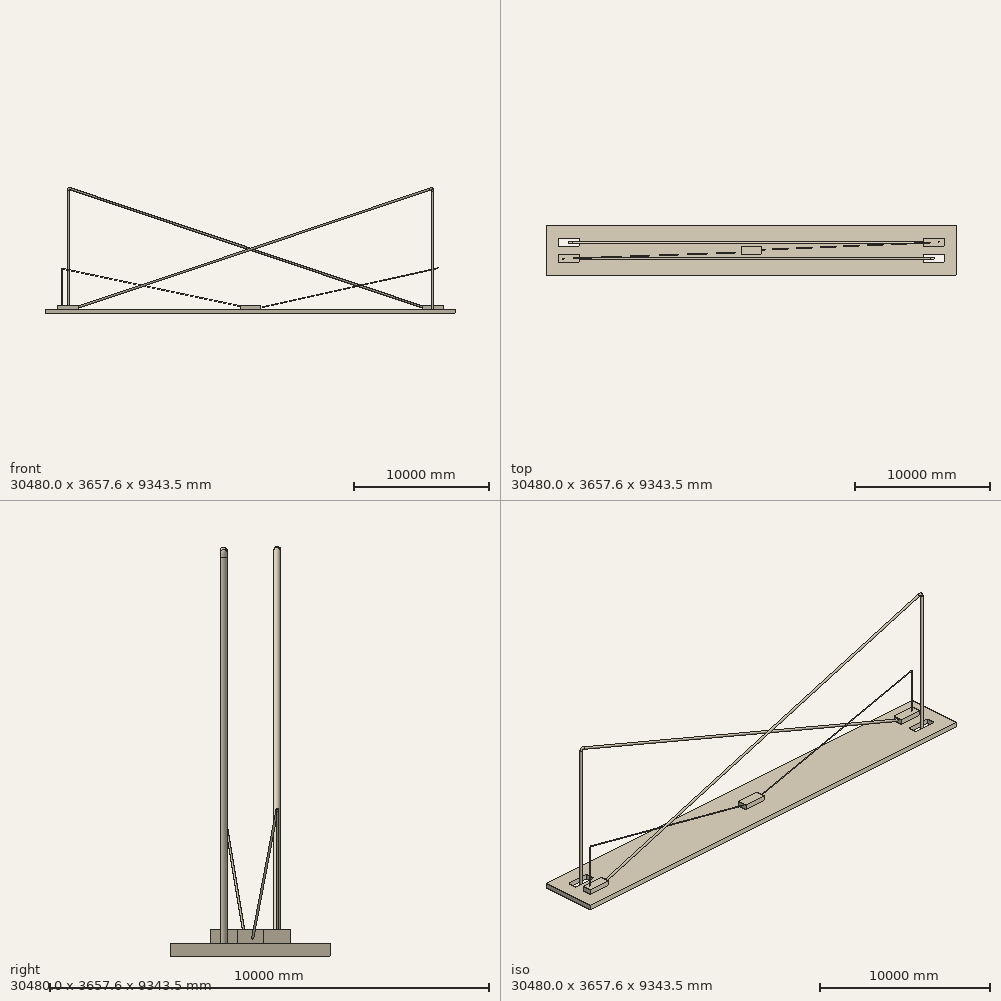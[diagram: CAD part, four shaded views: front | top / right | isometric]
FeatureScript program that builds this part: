
annotation { "Feature Type Name" : "Feature", "Feature Type Description" : "" }
export const myFeature = defineFeature(function(context is Context, id is Id, definition is map)
    precondition{}
    {
        {
            var Q0;
            Q0=qCreatedBy(makeId("Top.planeOp"),FACE);
            var sketch = newSketch(context, id + "F0", { "sketchPlane" : qUnion([Q0])});
            skLineSegment(sketch, "E0.bottom", {"start": v(15240, -1828.8) * mm, "end": v(-15240, -1828.8) * mm});
            skLineSegment(sketch, "E0.top", {"start": v(15240, 1828.8) * mm, "end": v(-15240, 1828.8) * mm});
            skLineSegment(sketch, "E0.left", {"start": v(15240, -1828.8) * mm, "end": v(15240, 1828.8) * mm});
            skLineSegment(sketch, "E0.right", {"start": v(-15240, -1828.8) * mm, "end": v(-15240, 1828.8) * mm});
            skPoint(sketch, "E0.middle", {"position": v(0, 0) * mm});
            skSolve(sketch);
        }
        {
            var Q0;
            Q0 = qSketchRegion(id + "F0", true);
            extrude(context, id + "F1", {"entities" : qUnion([Q0]), "depth" : 304.8 * mm, "offsetDistance" : 25.4 * mm});
        }
        {
            var Q0;
            Q0=makeQuery(id+"F1.opExtrude","CAP_FACE",FACE,{"disambiguationData":[OSD([sQuery(id+"F0.wireOp",EDGE,"E0.bottom"),sQuery(id+"F0.wireOp",EDGE,"E0.top"),sQuery(id+"F0.wireOp",EDGE,"E0.left"),sQuery(id+"F0.wireOp",EDGE,"E0.right")])],"isStart":false});
            var sketch = newSketch(context, id + "F2", { "sketchPlane" : qUnion([Q0])});
            skLineSegment(sketch, "E1", {"start": v(-17977.46, 914.4) * mm, "end": v(18300.4, 914.4) * mm, "construction": true});
            skLineSegment(sketch, "E2", {"start": v(-18010.1, -914.4) * mm, "end": v(18389.17, -914.4) * mm, "construction": true});
            skLineSegment(sketch, "E3", {"start": v(14325.6, 2510.02) * mm, "end": v(14325.6, -3119.62) * mm, "construction": true});
            skLineSegment(sketch, "E4", {"start": v(-14325.6, 2567.98) * mm, "end": v(-14325.6, -2658.46) * mm, "construction": true});
            skLineSegment(sketch, "E5.bottom", {"start": v(-14325.6, 914.4) * mm, "end": v(-12801.6, 914.4) * mm});
            skLineSegment(sketch, "E5.top", {"start": v(-14325.6, 304.8) * mm, "end": v(-12801.6, 304.8) * mm});
            skLineSegment(sketch, "E5.left", {"start": v(-14325.6, 914.4) * mm, "end": v(-14325.6, 304.8) * mm});
            skLineSegment(sketch, "E5.right", {"start": v(-12801.6, 914.4) * mm, "end": v(-12801.6, 304.8) * mm});
            skLineSegment(sketch, "E6.bottom", {"start": v(14325.6, -304.8) * mm, "end": v(12801.6, -304.8) * mm});
            skLineSegment(sketch, "E6.top", {"start": v(14325.6, -914.4) * mm, "end": v(12801.6, -914.4) * mm});
            skLineSegment(sketch, "E6.left", {"start": v(14325.6, -304.8) * mm, "end": v(14325.6, -914.4) * mm});
            skLineSegment(sketch, "E6.right", {"start": v(12801.6, -304.8) * mm, "end": v(12801.6, -914.4) * mm});
            skLineSegment(sketch, "E7.bottom", {"start": v(12801.6, 914.4) * mm, "end": v(14325.6, 914.4) * mm, "construction": true});
            skLineSegment(sketch, "E7.top", {"start": v(12801.6, 304.8) * mm, "end": v(14325.6, 304.8) * mm, "construction": true});
            skLineSegment(sketch, "E7.left", {"start": v(12801.6, 914.4) * mm, "end": v(12801.6, 304.8) * mm, "construction": true});
            skLineSegment(sketch, "E7.right", {"start": v(14325.6, 914.4) * mm, "end": v(14325.6, 304.8) * mm, "construction": true});
            skLineSegment(sketch, "E8.bottom", {"start": v(-14325.6, -304.8) * mm, "end": v(-12801.6, -304.8) * mm, "construction": true});
            skLineSegment(sketch, "E8.top", {"start": v(-14325.6, -914.4) * mm, "end": v(-12801.6, -914.4) * mm, "construction": true});
            skLineSegment(sketch, "E8.left", {"start": v(-14325.6, -304.8) * mm, "end": v(-14325.6, -914.4) * mm, "construction": true});
            skLineSegment(sketch, "E8.right", {"start": v(-12801.6, -304.8) * mm, "end": v(-12801.6, -914.4) * mm, "construction": true});
            skLineSegment(sketch, "E9.bottom", {"start": v(762, -304.8) * mm, "end": v(-762, -304.8) * mm});
            skLineSegment(sketch, "E9.top", {"start": v(762, 304.8) * mm, "end": v(-762, 304.8) * mm});
            skLineSegment(sketch, "E9.left", {"start": v(762, -304.8) * mm, "end": v(762, 304.8) * mm});
            skLineSegment(sketch, "E9.right", {"start": v(-762, -304.8) * mm, "end": v(-762, 304.8) * mm});
            skPoint(sketch, "E9.middle", {"position": v(0, 0) * mm});
            skLineSegment(sketch, "E10", {"start": v(12801.6, -609.6) * mm, "end": v(14325.6, -609.6) * mm, "construction": true});
            skLineSegment(sketch, "E11", {"start": v(13563.6, -304.8) * mm, "end": v(13563.6, -914.4) * mm, "construction": true});
            skSolve(sketch);
        }
        {
            var Q0;
            Q0 = qSketchRegion(id + "F2", true);
            extrude(context, id + "F3", {"entities" : qUnion([Q0]), "operationType" : NewBodyOperationType.REMOVE, "endBound" : BoundingType.THROUGH_ALL, "oppositeDirection" : true, "depth" : 25.4 * mm, "offsetDistance" : 25.4 * mm});
        }
        {
            var Q0;
            Q0=makeQuery(id+"F1.opExtrude","CAP_FACE",FACE,{"disambiguationData":[OSD([sQuery(id+"F0.wireOp",EDGE,"E0.bottom"),sQuery(id+"F0.wireOp",EDGE,"E0.top"),sQuery(id+"F0.wireOp",EDGE,"E0.left"),sQuery(id+"F0.wireOp",EDGE,"E0.right")])],"isStart":false});
            var sketch = newSketch(context, id + "F4", { "sketchPlane" : qUnion([Q0])});
            skLineSegment(sketch, "E12", {"start": v(-13563.6, 2097.28) * mm, "end": v(-13563.6, -1995.82) * mm, "construction": true});
            skLineSegment(sketch, "E13", {"start": v(-14593.28, 609.6) * mm, "end": v(-12270.27, 609.6) * mm, "construction": true});
            skCircle(sketch, "E14", {"center": v(-13563.6, 609.6) * mm, "radius": 76.2 * mm});
            skSolve(sketch);
        }
        {
            var Q0;
            Q0 = qSketchRegion(id + "F4", true);
            extrude(context, id + "F5", {"entities" : qUnion([Q0]), "depth" : 8839.2 * mm, "offsetDistance" : 25.4 * mm, "hasSecondDirection" : true, "secondDirectionOppositeDirection" : true, "secondDirectionDepth" : 304.8 * mm});
        }
        {
            var Q0;
            Q0=makeQuery(id+"F5.opExtrude","CAP_FACE",FACE,{"disambiguationData":[OSD([sQuery(id+"F4.wireOp",EDGE,"E14")])],"isStart":false});
            var sketch = newSketch(context, id + "F6", { "sketchPlane" : qUnion([Q0])});
            skLineSegment(sketch, "E15", {"start": v(-13563.6, 685.8) * mm, "end": v(-13563.6, 533.4) * mm, "construction": true});
            skLineSegment(sketch, "E16", {"start": v(-13639.8, 609.6) * mm, "end": v(-13487.4, 609.6) * mm, "construction": true});
            skSolve(sketch);
        }
        {
            var Q0;
            Q0=makeQuery(id+"F6.imprint","IMPRINT",FACE,{"disambiguationData":[TD([[makeQuery(id+"F6.imprint","IMPRINT",EDGE,{"derivedFrom":makeQuery(id+"F5.opExtrude","CAP_EDGE",EDGE,{"disambiguationData":[OSD([sQuery(id+"F4.wireOp",EDGE,"E14")])],"isStart":false})}),1.0]])]});
            var sketch = newSketch(context, id + "F7", { "sketchPlane" : qUnion([Q0])});
            skCircle(sketch, "E17", {"center": v(-13563.6, 609.6) * mm, "radius": 76.2 * mm});
            skSolve(sketch);
        }
        {
            var Q0;
            Q0=qCreatedBy(makeId("Front.planeOp"),FACE);
            cPlane(context, id + "F8", {"entities" : qUnion([Q0]), "cplaneType" : CPlaneType.OFFSET, "offset" : 609.6 * mm, "oppositeDirection" : true, "width" : 152.4 * mm, "height" : 152.4 * mm});
        }
        {
            var Q0;
            Q0=makeQuery(id+"F1.opExtrude","CAP_FACE",FACE,{"disambiguationData":[OSD([sQuery(id+"F0.wireOp",EDGE,"E0.bottom"),sQuery(id+"F0.wireOp",EDGE,"E0.top"),sQuery(id+"F0.wireOp",EDGE,"E0.left"),sQuery(id+"F0.wireOp",EDGE,"E0.right")])],"isStart":false});
            var sketch = newSketch(context, id + "F9", { "sketchPlane" : qUnion([Q0])});
            skLineSegment(sketch, "E18.bottom", {"start": v(12801.6, 914.4) * mm, "end": v(14325.6, 914.4) * mm});
            skLineSegment(sketch, "E18.top", {"start": v(12801.6, 304.8) * mm, "end": v(14325.6, 304.8) * mm});
            skLineSegment(sketch, "E18.left", {"start": v(12801.6, 914.4) * mm, "end": v(12801.6, 304.8) * mm});
            skLineSegment(sketch, "E18.right", {"start": v(14325.6, 914.4) * mm, "end": v(14325.6, 304.8) * mm});
            skSolve(sketch);
        }
        {
            var Q0;
            Q0=makeQuery(id+"F9.imprint","IMPRINT",FACE,{"disambiguationData":[TD([[makeQuery(id+"F9.imprint","IMPRINT",EDGE,{"derivedFrom":sQuery(id+"F9.wireOp",EDGE,"E18.bottom")}),-1.0]])]});
            extrude(context, id + "F10", {"entities" : qUnion([Q0]), "operationType" : NewBodyOperationType.ADD, "depth" : 304.8 * mm, "offsetDistance" : 25.4 * mm});
        }
        {
            var Q0;
            Q0=qCreatedBy(id+"F8.planeOp",FACE);
            var sketch = newSketch(context, id + "F11", { "sketchPlane" : qUnion([Q0])});
            skLineSegment(sketch, "E19", {"start": v(12795.68, 470.32) * mm, "end": v(-13306.6, 9230.54) * mm});
            skLineSegment(sketch, "E20", {"start": v(12795.68, 470.32) * mm, "end": v(11705.65, 470.32) * mm, "construction": true});
            skSolve(sketch);
        }
        {
            var Q0;
            Q0=makeQuery(id+"F10.opExtrude","SWEPT_FACE",FACE,{"disambiguationData":[OSD([sQuery(id+"F9.wireOp",EDGE,"E18.left")])]});
            var Q1;
            Q1=makeQuery(id+"F10.opExtrude","CAP_EDGE",EDGE,{"disambiguationData":[OSD([sQuery(id+"F9.wireOp",EDGE,"E18.left")])],"isStart":false});
            cPlane(context, id + "F12", {"entities" : qUnion([Q0, Q1]), "cplaneType" : CPlaneType.LINE_ANGLE, "offset" : 25.4 * mm, "angle" : 18.55 * degree, "oppositeDirection" : true, "width" : 152.4 * mm, "height" : 152.4 * mm});
        }
        {
            var Q0;
            Q0=qCreatedBy(id+"F12.planeOp",FACE);
            var sketch = newSketch(context, id + "F13", { "sketchPlane" : qUnion([Q0])});
            skCircle(sketch, "E21", {"center": v(609.6, 4516.6) * mm, "radius": 76.2 * mm});
            skSolve(sketch);
        }
        {
            var Q0;
            Q0=makeQuery(id+"F13.imprint","IMPRINT",FACE,{"disambiguationData":[TD([[makeQuery(id+"F13.imprint","IMPRINT",EDGE,{"derivedFrom":sQuery(id+"F13.wireOp",EDGE,"E21")}),1.0]])]});
            var Q1;
            Q1=makeQuery(id+"F10.opExtrude","SWEPT_FACE",FACE,{"disambiguationData":[OSD([sQuery(id+"F9.wireOp",EDGE,"E18.left")])]});
            extrude(context, id + "F14", {"entities" : qUnion([Q0]), "operationType" : NewBodyOperationType.ADD, "endBound" : BoundingType.UP_TO_SURFACE, "depth" : 25.4 * mm, "endBoundEntityFace" : qUnion([Q1]), "offsetDistance" : 25.4 * mm, "hasSecondDirection" : true, "secondDirectionOppositeDirection" : true, "secondDirectionDepth" : 27533.6 * mm});
        }
        {
            var Q0;
            Q0=makeQuery(id+"F14.opExtrude","CAP_FACE",FACE,{"disambiguationData":[OSD([sQuery(id+"F13.wireOp",EDGE,"E21")])],"isStart":true});
            var sketch = newSketch(context, id + "F15", { "sketchPlane" : qUnion([Q0])});
            skLineSegment(sketch, "E22", {"start": v(-609.6, 4592.8) * mm, "end": v(-609.6, 4440.4) * mm, "construction": true});
            skLineSegment(sketch, "E23", {"start": v(-685.8, 4516.6) * mm, "end": v(-533.4, 4516.6) * mm, "construction": true});
            skSolve(sketch);
        }
        {
            var Q0;
            Q0=qCreatedBy(id+"F8.planeOp",FACE);
            var sketch = newSketch(context, id + "F16", { "sketchPlane" : qUnion([Q0])});
            skFitSpline(sketch, "E24", {"points": [v(-13563.6, 9144) * mm, v(-13557.89, 9195.2) * mm, v(-13517.9, 9248.03) * mm, v(-13451.5, 9267.3) * mm, v(-13385.25, 9253.96) * mm, v(-13344.14, 9241.96) * mm], "startDerivative": vector(-5.95, 210.42) * mm, "endDerivative": vector(230.57, -66.68) * mm});
            skSolve(sketch);
        }
        {
            var Q0;
            Q0=makeQuery(id+"F7.imprint","IMPRINT",FACE,{"disambiguationData":[TD([[makeQuery(id+"F7.imprint","IMPRINT",EDGE,{"derivedFrom":sQuery(id+"F7.wireOp",EDGE,"E17")}),1.0]])]});
            var Q1;
            Q1=sQuery(id+"F16.wireOp",EDGE,"E24");
            sweep(context, id + "F17", {"profiles" : qUnion([Q0]), "path" : qUnion([Q1])});
        }
        {
            var Q0;
            Q0=makeQuery(id+"F10.opExtrude","CAP_FACE",FACE,{"disambiguationData":[OSD([sQuery(id+"F9.wireOp",EDGE,"E18.bottom"),sQuery(id+"F9.wireOp",EDGE,"E18.top"),sQuery(id+"F9.wireOp",EDGE,"E18.left"),sQuery(id+"F9.wireOp",EDGE,"E18.right")])],"isStart":false});
            var sketch = newSketch(context, id + "F18", { "sketchPlane" : qUnion([Q0])});
            skLineSegment(sketch, "E25", {"start": v(12801.6, 609.6) * mm, "end": v(14325.6, 609.6) * mm, "construction": true});
            skCircle(sketch, "E26", {"center": v(13970, 609.6) * mm, "radius": 25.4 * mm});
            skSolve(sketch);
        }
        {
            var Q0;
            Q0=makeQuery(id+"F18.imprint","IMPRINT",FACE,{"disambiguationData":[TD([[makeQuery(id+"F18.imprint","IMPRINT",EDGE,{"derivedFrom":sQuery(id+"F18.wireOp",EDGE,"E26")}),1.0]])]});
            var Q1;
            Q1 = qConstructionFilter(qBodyType(qCreatedBy(id + "F18" ,EDGE), BodyType.WIRE), ConstructionObject.NO);
            extrude(context, id + "F19", {"entities" : qUnion([Q0]), "surfaceEntities" : qUnion([Q1]), "depth" : 2692.4 * mm, "offsetDistance" : 25.4 * mm});
        }
        {
            var Q0;
            Q0=makeQuery(id+"F1.opExtrude","CAP_FACE",FACE,{"disambiguationData":[OSD([sQuery(id+"F0.wireOp",EDGE,"E0.bottom"),sQuery(id+"F0.wireOp",EDGE,"E0.top"),sQuery(id+"F0.wireOp",EDGE,"E0.left"),sQuery(id+"F0.wireOp",EDGE,"E0.right")])],"isStart":false});
            var sketch = newSketch(context, id + "F20", { "sketchPlane" : qUnion([Q0])});
            skLineSegment(sketch, "E27", {"start": v(12801.6, -609.6) * mm, "end": v(14325.6, -609.6) * mm, "construction": true});
            skLineSegment(sketch, "E28", {"start": v(13563.6, -304.8) * mm, "end": v(13563.6, -914.4) * mm, "construction": true});
            skCircle(sketch, "E29", {"center": v(13563.6, -609.6) * mm, "radius": 76.2 * mm});
            skSolve(sketch);
        }
        {
            var Q0;
            Q0 = qSketchRegion(id + "F20", true);
            extrude(context, id + "F21", {"entities" : qUnion([Q0]), "depth" : 8788.4 * mm, "offsetDistance" : 25.4 * mm, "hasSecondDirection" : true, "secondDirectionOppositeDirection" : true, "secondDirectionDepth" : 304.8 * mm});
        }
        {
            var Q0;
            Q0=makeQuery(id+"F1.opExtrude","CAP_FACE",FACE,{"disambiguationData":[OSD([sQuery(id+"F0.wireOp",EDGE,"E0.bottom"),sQuery(id+"F0.wireOp",EDGE,"E0.top"),sQuery(id+"F0.wireOp",EDGE,"E0.left"),sQuery(id+"F0.wireOp",EDGE,"E0.right")])],"isStart":false});
            var sketch = newSketch(context, id + "F22", { "sketchPlane" : qUnion([Q0])});
            skLineSegment(sketch, "E30.bottom", {"start": v(-14325.6, -304.8) * mm, "end": v(-12801.6, -304.8) * mm});
            skLineSegment(sketch, "E30.top", {"start": v(-14325.6, -914.4) * mm, "end": v(-12801.6, -914.4) * mm});
            skLineSegment(sketch, "E30.left", {"start": v(-14325.6, -304.8) * mm, "end": v(-14325.6, -914.4) * mm});
            skLineSegment(sketch, "E30.right", {"start": v(-12801.6, -304.8) * mm, "end": v(-12801.6, -914.4) * mm});
            skSolve(sketch);
        }
        {
            var Q0;
            Q0 = qSketchRegion(id + "F22", true);
            extrude(context, id + "F23", {"entities" : qUnion([Q0]), "operationType" : NewBodyOperationType.ADD, "depth" : 304.8 * mm, "offsetDistance" : 25.4 * mm});
        }
        {
            var Q0;
            Q0=makeQuery(id+"F23.opExtrude","SWEPT_FACE",FACE,{"disambiguationData":[OSD([sQuery(id+"F22.wireOp",EDGE,"E30.right")])]});
            var Q1;
            Q1=makeQuery(id+"F23.opExtrude","CAP_EDGE",EDGE,{"disambiguationData":[OSD([sQuery(id+"F22.wireOp",EDGE,"E30.right")])],"isStart":false});
            cPlane(context, id + "F24", {"entities" : qUnion([Q0, Q1]), "cplaneType" : CPlaneType.LINE_ANGLE, "offset" : 25.4 * mm, "angle" : 18.55 * degree, "width" : 152.4 * mm, "height" : 152.4 * mm});
        }
        {
            var Q0;
            Q0=qCreatedBy(id+"F8.planeOp",FACE);
            cPlane(context, id + "F25", {"entities" : qUnion([Q0]), "cplaneType" : CPlaneType.OFFSET, "offset" : 1219.2 * mm, "width" : 152.4 * mm, "height" : 152.4 * mm});
        }
        {
            var Q0;
            Q0=qCreatedBy(id+"F24.planeOp",FACE);
            var sketch = newSketch(context, id + "F26", { "sketchPlane" : qUnion([Q0])});
            skCircle(sketch, "E31", {"center": v(609.6, 4498.13) * mm, "radius": 76.2 * mm});
            skSolve(sketch);
        }
        {
            var Q0;
            Q0=makeQuery(id+"F26.imprint","IMPRINT",FACE,{"disambiguationData":[TD([[makeQuery(id+"F26.imprint","IMPRINT",EDGE,{"derivedFrom":sQuery(id+"F26.wireOp",EDGE,"E31")}),1.0]])]});
            var Q1;
            Q1=makeQuery(id+"F23.opExtrude","SWEPT_FACE",FACE,{"disambiguationData":[OSD([sQuery(id+"F22.wireOp",EDGE,"E30.right")])]});
            extrude(context, id + "F27", {"entities" : qUnion([Q0]), "operationType" : NewBodyOperationType.ADD, "oppositeDirection" : true, "depth" : 27508.2 * mm, "offsetDistance" : 25.4 * mm, "hasSecondDirection" : true, "secondDirectionBound" : SecondDirectionBoundingType.UP_TO_SURFACE, "secondDirectionOppositeDirection" : false, "secondDirectionDepth" : 25.4 * mm, "secondDirectionBoundEntityFace" : qUnion([Q1])});
        }
        {
            var Q0;
            Q0=makeQuery(id+"F21.opExtrude","CAP_FACE",FACE,{"disambiguationData":[OSD([sQuery(id+"F20.wireOp",EDGE,"E29")])],"isStart":false});
            var sketch = newSketch(context, id + "F28", { "sketchPlane" : qUnion([Q0])});
            skLineSegment(sketch, "E32", {"start": v(13563.6, -533.4) * mm, "end": v(13563.6, -685.8) * mm, "construction": true});
            skLineSegment(sketch, "E33", {"start": v(13487.4, -609.6) * mm, "end": v(13639.8, -609.6) * mm, "construction": true});
            skSolve(sketch);
        }
        {
            var Q0;
            {var subQ0=sQuery(id+"F26.wireOp",EDGE,"E31");Q0=makeQuery(id+"F27.opExtrude","CAP_FACE",FACE,{"disambiguationData":[OSD([subQ0]),topologyDisambiguationEdgeConnected([makeQuery(id+"F26.imprint","IMPRINT",EDGE,{"derivedFrom":subQ0})])],"isStart":false});}
            var sketch = newSketch(context, id + "F29", { "sketchPlane" : qUnion([Q0])});
            skLineSegment(sketch, "E34", {"start": v(-533.4, 4498.13) * mm, "end": v(-685.8, 4498.13) * mm, "construction": true});
            skLineSegment(sketch, "E35", {"start": v(-609.6, 4574.33) * mm, "end": v(-609.6, 4421.93) * mm, "construction": true});
            skSolve(sketch);
        }
        {
            var Q0;
            Q0=qCreatedBy(id+"F25.planeOp",FACE);
            var sketch = newSketch(context, id + "F30", { "sketchPlane" : qUnion([Q0])});
            skFitSpline(sketch, "E36", {"points": [v(13325.93, 9216.36) * mm, v(13389.39, 9235.5) * mm, v(13462.23, 9248.26) * mm, v(13530.33, 9233.42) * mm, v(13556.5, 9195.8) * mm, v(13562.3, 9149.55) * mm, v(13563.6, 9093.2) * mm], "startDerivative": vector(362.98, 130.88) * mm, "endDerivative": vector(2.68, -321.12) * mm});
            skSolve(sketch);
        }
        {
            var Q0;
            {var subQ0=sQuery(id+"F26.wireOp",EDGE,"E31");Q0=makeQuery(id+"F29.imprint","IMPRINT",FACE,{"disambiguationData":[TD([[makeQuery(id+"F29.imprint","IMPRINT",EDGE,{"derivedFrom":makeQuery(id+"F27.opExtrude","CAP_EDGE",EDGE,{"disambiguationData":[OSD([subQ0]),topologyDisambiguationEdgeConnected([makeQuery(id+"F26.imprint","IMPRINT",EDGE,{"derivedFrom":subQ0})])],"isStart":false})}),-1.0]])]});}
            var Q1;
            Q1=sQuery(id+"F30.wireOp",EDGE,"E36");
            sweep(context, id + "F31", {"profiles" : qUnion([Q0]), "path" : qUnion([Q1])});
        }
        {
            var Q0;
            Q0=makeQuery(id+"F1.opExtrude","CAP_FACE",FACE,{"disambiguationData":[OSD([sQuery(id+"F0.wireOp",EDGE,"E0.bottom"),sQuery(id+"F0.wireOp",EDGE,"E0.top"),sQuery(id+"F0.wireOp",EDGE,"E0.left"),sQuery(id+"F0.wireOp",EDGE,"E0.right")])],"isStart":false});
            var sketch = newSketch(context, id + "F32", { "sketchPlane" : qUnion([Q0])});
            skLineSegment(sketch, "E37.bottom", {"start": v(-762, -304.8) * mm, "end": v(762, -304.8) * mm});
            skLineSegment(sketch, "E37.top", {"start": v(-762, 304.8) * mm, "end": v(762, 304.8) * mm});
            skLineSegment(sketch, "E37.left", {"start": v(-762, -304.8) * mm, "end": v(-762, 304.8) * mm});
            skLineSegment(sketch, "E37.right", {"start": v(762, -304.8) * mm, "end": v(762, 304.8) * mm});
            skSolve(sketch);
        }
        {
            var Q0;
            Q0 = qSketchRegion(id + "F32", true);
            extrude(context, id + "F33", {"entities" : qUnion([Q0]), "depth" : 304.8 * mm, "offsetDistance" : 25.4 * mm});
        }
        {
            var Q0;
            Q0=makeQuery(id+"F19.opExtrude","CAP_FACE",FACE,{"disambiguationData":[OSD([sQuery(id+"F18.wireOp",EDGE,"E26")])],"isStart":false});
            var sketch = newSketch(context, id + "F34", { "sketchPlane" : qUnion([Q0])});
            skLineSegment(sketch, "E38", {"start": v(13944.6, 609.6) * mm, "end": v(13995.4, 609.6) * mm, "construction": true});
            skLineSegment(sketch, "E39", {"start": v(13968.93, 634.98) * mm, "end": v(13971.07, 584.22) * mm, "construction": true});
            skLineSegment(sketch, "E40", {"start": v(13995.38, 610.67) * mm, "end": v(13944.62, 608.53) * mm, "construction": true});
            skSolve(sketch);
        }
        {
            var Q0;
            Q0=makeQuery(id+"F34.imprint","IMPRINT",FACE,{"disambiguationData":[TD([[makeQuery(id+"F34.imprint","IMPRINT",EDGE,{"derivedFrom":makeQuery(id+"F19.opExtrude","CAP_EDGE",EDGE,{"disambiguationData":[OSD([sQuery(id+"F18.wireOp",EDGE,"E26")])],"isStart":false})}),1.0]])]});
            cPlane(context, id + "F35", {"entities" : qUnion([Q0]), "cplaneType" : CPlaneType.OFFSET, "offset" : 50.8 * mm, "width" : 152.4 * mm, "height" : 152.4 * mm});
        }
        {
            var Q0;
            Q0=qCreatedBy(id+"F35.planeOp",FACE);
            var sketch = newSketch(context, id + "F36", { "sketchPlane" : qUnion([Q0])});
            skLineSegment(sketch, "E41", {"start": v(13968.93, 634.98) * mm, "end": v(13971.07, 584.22) * mm, "construction": true});
            skSolve(sketch);
        }
        {
            var Q0;
            Q0=sQuery(id+"F36.wireOp",EDGE,"E41");
            var Q1;
            Q1=makeQuery(id+"F1.opExtrude","CAP_FACE",FACE,{"disambiguationData":[OSD([sQuery(id+"F0.wireOp",EDGE,"E0.bottom"),sQuery(id+"F0.wireOp",EDGE,"E0.top"),sQuery(id+"F0.wireOp",EDGE,"E0.left"),sQuery(id+"F0.wireOp",EDGE,"E0.right")])],"isStart":false});
            cPlane(context, id + "F37", {"entities" : qUnion([Q0, Q1]), "cplaneType" : CPlaneType.LINE_ANGLE, "offset" : 25.4 * mm, "angle" : 77.5 * degree, "oppositeDirection" : true, "width" : 152.4 * mm, "height" : 152.4 * mm});
        }
        {
            var Q0;
            Q0=sQuery(id+"F34.wireOp",EDGE,"E40");
            var Q1;
            Q1=makeQuery(id+"F1.opExtrude","CAP_FACE",FACE,{"disambiguationData":[OSD([sQuery(id+"F0.wireOp",EDGE,"E0.bottom"),sQuery(id+"F0.wireOp",EDGE,"E0.top"),sQuery(id+"F0.wireOp",EDGE,"E0.left"),sQuery(id+"F0.wireOp",EDGE,"E0.right")])],"isStart":false});
            cPlane(context, id + "F38", {"entities" : qUnion([Q0, Q1]), "cplaneType" : CPlaneType.LINE_ANGLE, "offset" : 25.4 * mm, "angle" : 90 * degree, "width" : 152.4 * mm, "height" : 152.4 * mm});
        }
        {
            var Q0;
            Q0=qCreatedBy(id+"F37.planeOp",FACE);
            cPlane(context, id + "F39", {"entities" : qUnion([Q0]), "cplaneType" : CPlaneType.OFFSET, "offset" : 50.8 * mm, "width" : 152.4 * mm, "height" : 152.4 * mm});
        }
        {
            var Q0;
            Q0=qCreatedBy(id+"F39.planeOp",FACE);
            var sketch = newSketch(context, id + "F40", { "sketchPlane" : qUnion([Q0])});
            skCircle(sketch, "E42", {"center": v(-16.92, 246.95) * mm, "radius": 25.4 * mm});
            skSolve(sketch);
        }
        {
            var Q0;
            Q0 = qSketchRegion(id + "F40", true);
            extrude(context, id + "F41", {"entities" : qUnion([Q0]), "operationType" : NewBodyOperationType.ADD, "endBound" : BoundingType.UP_TO_NEXT, "depth" : 25.4 * mm, "offsetDistance" : 25.4 * mm});
        }
        {
            var Q0;
            Q0=makeQuery(id+"F41.opExtrude","CAP_FACE",FACE,{"disambiguationData":[OSD([sQuery(id+"F40.wireOp",EDGE,"E42")])],"isStart":true});
            var sketch = newSketch(context, id + "F42", { "sketchPlane" : qUnion([Q0])});
            skLineSegment(sketch, "E43", {"start": v(-1.84, 264.08) * mm, "end": v(35.68, 229.83) * mm, "construction": true});
            skLineSegment(sketch, "E44", {"start": v(-0.2, 228.2) * mm, "end": v(34.05, 265.72) * mm, "construction": true});
            skSolve(sketch);
        }
        {
            var Q0;
            Q0=qCreatedBy(id+"F38.planeOp",FACE);
            var sketch = newSketch(context, id + "F43", { "sketchPlane" : qUnion([Q0])});
            skFitSpline(sketch, "E45", {"points": [v(13983.28, 3302) * mm, v(13980.36, 3327.16) * mm, v(13972.6, 3340.3) * mm, v(13960.9, 3345.86) * mm, v(13948.48, 3345.39) * mm, v(13933.69, 3341.8) * mm], "startDerivative": vector(-2.2, 65.07) * mm, "endDerivative": vector(-67.3, -13.02) * mm});
            skSolve(sketch);
        }
        {
            var Q0;
            Q0=makeQuery(id+"F34.imprint","IMPRINT",FACE,{"disambiguationData":[TD([[makeQuery(id+"F34.imprint","IMPRINT",EDGE,{"derivedFrom":makeQuery(id+"F19.opExtrude","CAP_EDGE",EDGE,{"disambiguationData":[OSD([sQuery(id+"F18.wireOp",EDGE,"E26")])],"isStart":false})}),1.0]])]});
            var Q1;
            Q1=sQuery(id+"F43.wireOp",EDGE,"E45");
            sweep(context, id + "F44", {"profiles" : qUnion([Q0]), "path" : qUnion([Q1])});
        }
        {
            var Q0;
            Q0=makeQuery(id+"F23.opExtrude","CAP_FACE",FACE,{"disambiguationData":[OSD([sQuery(id+"F22.wireOp",EDGE,"E30.bottom"),sQuery(id+"F22.wireOp",EDGE,"E30.top"),sQuery(id+"F22.wireOp",EDGE,"E30.left"),sQuery(id+"F22.wireOp",EDGE,"E30.right")])],"isStart":false});
            var sketch = newSketch(context, id + "F45", { "sketchPlane" : qUnion([Q0])});
            skCircle(sketch, "E46", {"center": v(-14020.8, -609.6) * mm, "radius": 25.4 * mm});
            skSolve(sketch);
        }
        {
            var Q0;
            Q0 = qSketchRegion(id + "F45", true);
            extrude(context, id + "F46", {"entities" : qUnion([Q0]), "operationType" : NewBodyOperationType.ADD, "depth" : 2667 * mm, "offsetDistance" : 25.4 * mm});
        }
        {
            var Q0;
            Q0=makeQuery(id+"F46.opExtrude","CAP_FACE",FACE,{"disambiguationData":[OSD([sQuery(id+"F45.wireOp",EDGE,"E46")])],"isStart":false});
            var sketch = newSketch(context, id + "F47", { "sketchPlane" : qUnion([Q0])});
            skLineSegment(sketch, "E47", {"start": v(-13995.4, -609.6) * mm, "end": v(-14046.2, -609.6) * mm, "construction": true});
            skLineSegment(sketch, "E48", {"start": v(-14020.92, -635) * mm, "end": v(-14020.92, -584.2) * mm, "construction": true});
            skLineSegment(sketch, "E49", {"start": v(-13995.42, -608.71) * mm, "end": v(-14046.18, -610.49) * mm, "construction": true});
            skSolve(sketch);
        }
        {
            var Q0;
            Q0=sQuery(id+"F47.wireOp",EDGE,"E48");
            var Q1;
            Q1=sQuery(id+"F47.wireOp",EDGE,"E47");
            cPlane(context, id + "F48", {"entities" : qUnion([Q0, Q1]), "cplaneType" : CPlaneType.LINE_ANGLE, "offset" : 25.4 * mm, "angle" : 90 * degree, "width" : 152.4 * mm, "height" : 152.4 * mm});
        }
        {
            var Q0;
            Q0=qCreatedBy(id+"F48.planeOp",FACE);
            var Q1;
            Q1=sQuery(id+"F47.wireOp",EDGE,"E49");
            cPlane(context, id + "F49", {"entities" : qUnion([Q0, Q1]), "cplaneType" : CPlaneType.LINE_ANGLE, "offset" : 25.4 * mm, "angle" : 0 * degree, "width" : 152.4 * mm, "height" : 152.4 * mm});
        }
        {
            var Q0;
            Q0=makeQuery(id+"F47.imprint","IMPRINT",FACE,{"disambiguationData":[TD([[makeQuery(id+"F47.imprint","IMPRINT",EDGE,{"derivedFrom":makeQuery(id+"F46.opExtrude","CAP_EDGE",EDGE,{"disambiguationData":[OSD([sQuery(id+"F45.wireOp",EDGE,"E46")])],"isStart":false})}),1.0]])]});
            cPlane(context, id + "F50", {"entities" : qUnion([Q0]), "cplaneType" : CPlaneType.OFFSET, "offset" : 50.8 * mm, "width" : 152.4 * mm, "height" : 152.4 * mm});
        }
        {
            var Q0;
            Q0=qCreatedBy(id+"F50.planeOp",FACE);
            var sketch = newSketch(context, id + "F51", { "sketchPlane" : qUnion([Q0])});
            skLineSegment(sketch, "E50", {"start": v(-14020.92, -635) * mm, "end": v(-14020.92, -584.2) * mm, "construction": true});
            skCircle(sketch, "E51", {"center": v(-14020.92, -609.6) * mm, "radius": 25.4 * mm, "construction": true});
            skLineSegment(sketch, "E52", {"start": v(-14020.04, -634.98) * mm, "end": v(-14021.8, -584.22) * mm, "construction": true});
            skSolve(sketch);
        }
        {
            var Q0;
            Q0=qCreatedBy(id+"F50.planeOp",FACE);
            var Q1;
            Q1=sQuery(id+"F51.wireOp",EDGE,"E52");
            cPlane(context, id + "F52", {"entities" : qUnion([Q0, Q1]), "cplaneType" : CPlaneType.LINE_ANGLE, "offset" : 25.4 * mm, "angle" : 78.11 * degree, "oppositeDirection" : true, "width" : 152.4 * mm, "height" : 152.4 * mm});
        }
        {
            var Q0;
            Q0=qCreatedBy(id+"F52.planeOp",FACE);
            cPlane(context, id + "F53", {"entities" : qUnion([Q0]), "cplaneType" : CPlaneType.OFFSET, "offset" : 63.5 * mm, "width" : 152.4 * mm, "height" : 152.4 * mm});
        }
        {
            var Q0;
            Q0=qCreatedBy(id+"F53.planeOp",FACE);
            var sketch = newSketch(context, id + "F54", { "sketchPlane" : qUnion([Q0])});
            skCircle(sketch, "E53", {"center": v(-117.28, 365.46) * mm, "radius": 25.4 * mm});
            skSolve(sketch);
        }
        {
            var Q0;
            Q0=makeQuery(id+"F54.imprint","IMPRINT",FACE,{"disambiguationData":[TD([[makeQuery(id+"F54.imprint","IMPRINT",EDGE,{"derivedFrom":sQuery(id+"F54.wireOp",EDGE,"E53")}),1.0]])]});
            extrude(context, id + "F55", {"entities" : qUnion([Q0]), "operationType" : NewBodyOperationType.ADD, "endBound" : BoundingType.UP_TO_NEXT, "depth" : 25.4 * mm, "offsetDistance" : 25.4 * mm});
        }
        {
            var Q0;
            Q0=makeQuery(id+"F55.opExtrude","CAP_FACE",FACE,{"disambiguationData":[OSD([sQuery(id+"F54.wireOp",EDGE,"E53")])],"isStart":true});
            var sketch = newSketch(context, id + "F56", { "sketchPlane" : qUnion([Q0])});
            skLineSegment(sketch, "E54", {"start": v(117.28, 340.06) * mm, "end": v(117.28, 390.86) * mm, "construction": true});
            skLineSegment(sketch, "E55", {"start": v(91.88, 365.46) * mm, "end": v(142.68, 365.46) * mm, "construction": true});
            skSolve(sketch);
        }
        {
            var Q0;
            Q0=qCreatedBy(id+"F49.planeOp",FACE);
            var sketch = newSketch(context, id + "F57", { "sketchPlane" : qUnion([Q0])});
            skFitSpline(sketch, "E56", {"points": [v(14033.53, 3276.6) * mm, v(14032.75, 3285.27) * mm, v(14028.15, 3297.5) * mm, v(14018.3, 3309.6) * mm, v(14003.35, 3315.31) * mm, v(13984.9, 3315.63) * mm, v(13971.52, 3314.32) * mm], "startDerivative": vector(0.02, 59.45) * mm, "endDerivative": vector(-97.55, -12.7) * mm});
            skSolve(sketch);
        }
        {
            var Q0;
            Q0=makeQuery(id+"F47.imprint","IMPRINT",FACE,{"disambiguationData":[TD([[makeQuery(id+"F47.imprint","IMPRINT",EDGE,{"derivedFrom":makeQuery(id+"F46.opExtrude","CAP_EDGE",EDGE,{"disambiguationData":[OSD([sQuery(id+"F45.wireOp",EDGE,"E46")])],"isStart":false})}),1.0]])]});
            var Q1;
            Q1=sQuery(id+"F57.wireOp",EDGE,"E56");
            sweep(context, id + "F58", {"profiles" : qUnion([Q0]), "path" : qUnion([Q1])});
        }
    });
